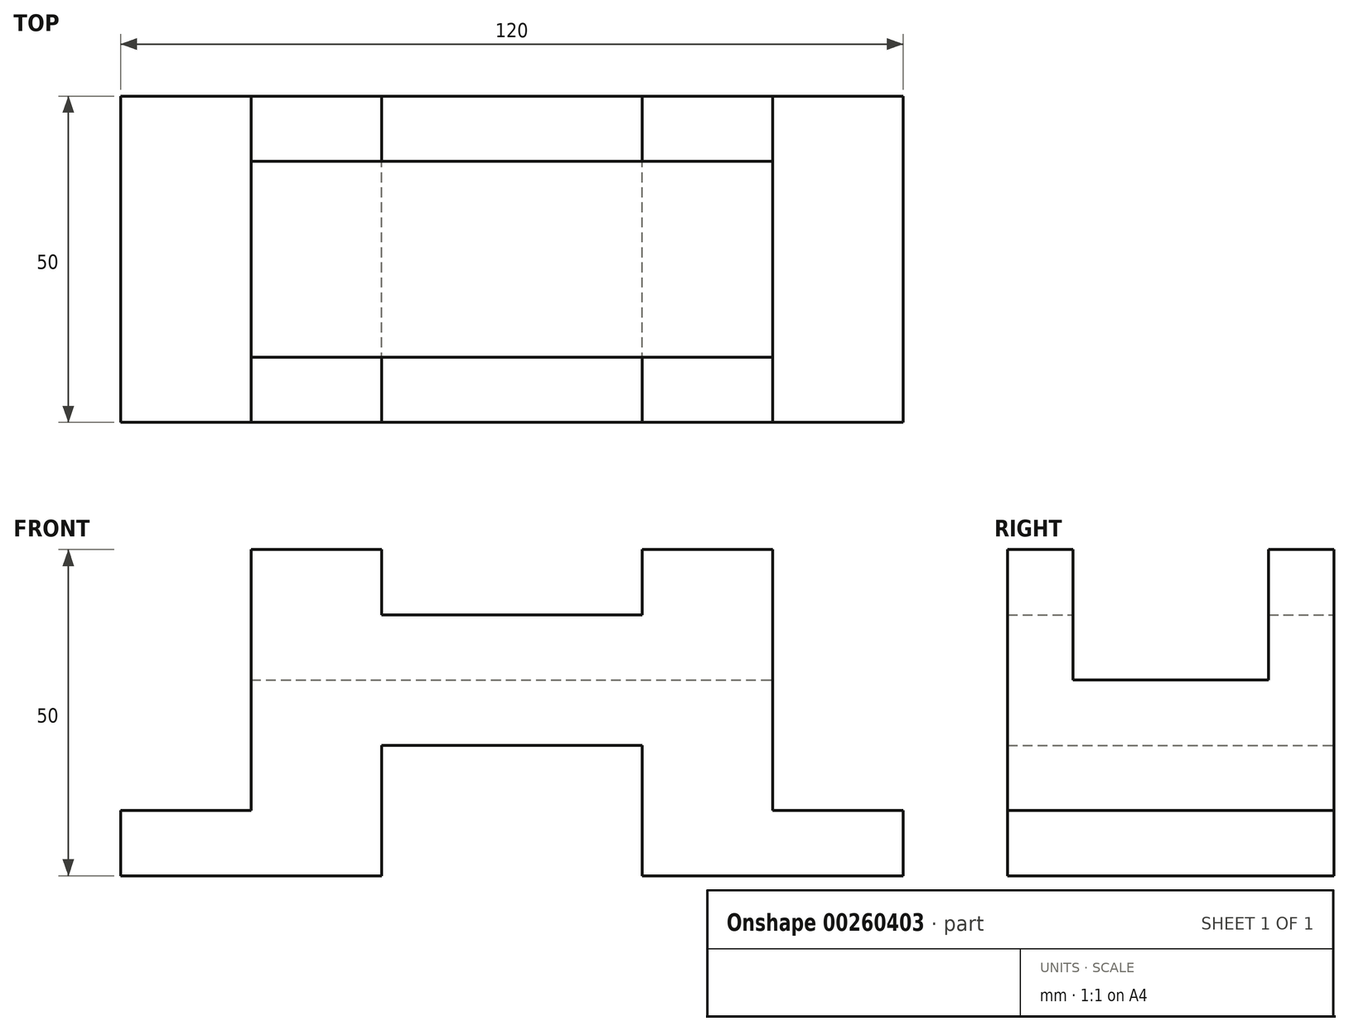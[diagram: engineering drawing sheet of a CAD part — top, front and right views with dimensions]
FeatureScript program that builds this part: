
annotation { "Feature Type Name" : "Feature", "Feature Type Description" : "" }
export const myFeature = defineFeature(function(context is Context, id is Id, definition is map)
    precondition{}
    {
        {
            assignVariable(context, id + "F0", {"name" : "A", "anyValue" : 50});
        }
        {
            var Q0;
            Q0=qCreatedBy(makeId("Front.planeOp"),FACE);
            var sketch = newSketch(context, id + "F1", { "sketchPlane" : qUnion([Q0])});
            skLineSegment(sketch, "E0", {"start": v(-0.57, -0.86) * mm, "end": v(0, 0) * mm});
            skLineSegment(sketch, "E1", {"start": v(-19.8, 0) * mm, "end": v(-19.8, 20) * mm});
            skLineSegment(sketch, "E2", {"start": v(20.2, 0) * mm, "end": v(20.2, 20) * mm});
            skLineSegment(sketch, "E3", {"start": v(-19.8, 20) * mm, "end": v(20.2, 20) * mm});
            skLineSegment(sketch, "E4", {"start": v(-19.8, 0) * mm, "end": v(-59.8, 0) * mm});
            skLineSegment(sketch, "E5", {"start": v(20.2, 0) * mm, "end": v(60.2, 0) * mm});
            skLineSegment(sketch, "E6", {"start": v(-59.8, 0) * mm, "end": v(60.2, 0) * mm});
            skLineSegment(sketch, "E7", {"start": v(60.2, 0) * mm, "end": v(60.2, 10) * mm});
            skLineSegment(sketch, "E8", {"start": v(-59.8, 0) * mm, "end": v(-59.8, 10) * mm});
            skLineSegment(sketch, "E9", {"start": v(60.2, 10) * mm, "end": v(40.2, 10) * mm});
            skLineSegment(sketch, "E10", {"start": v(40.2, 50) * mm, "end": v(40.2, 10) * mm});
            skLineSegment(sketch, "E11", {"start": v(-59.8, 10) * mm, "end": v(-39.8, 10) * mm});
            skLineSegment(sketch, "E12", {"start": v(-39.8, 10) * mm, "end": v(-39.8, 50) * mm});
            skLineSegment(sketch, "E13", {"start": v(-39.8, 50) * mm, "end": v(-19.8, 50) * mm});
            skLineSegment(sketch, "E14", {"start": v(-19.8, 40) * mm, "end": v(20.2, 40) * mm});
            skLineSegment(sketch, "E15", {"start": v(20.2, 40) * mm, "end": v(20.2, 50) * mm});
            skLineSegment(sketch, "E16", {"start": v(20.2, 50) * mm, "end": v(40.2, 50) * mm});
            skLineSegment(sketch, "E17", {"start": v(-19.8, 40) * mm, "end": v(-19.8, 50) * mm});
            skSolve(sketch);
        }
        {
            var Q0;
            {var subQ1=sQuery(id+"F1.wireOp",EDGE,"E1");Q0=makeQuery(id+"F1.imprint","IMPRINT",FACE,{"disambiguationData":[TD([[makeQuery(id+"F1.imprint","IMPRINT",EDGE,{"derivedFrom":subQ1}),1.0]])]});}
            extrude(context, id + "F2", {"entities" : qUnion([Q0]), "endBound" : BoundingType.SYMMETRIC, "depth" : (getVariable(context, 'A')) * mm});
        }
        {
            var Q0;
            Q0=makeQuery(id+"F2.opExtrude","SWEPT_FACE",FACE,{"disambiguationData":[OSD([sQuery(id+"F1.wireOp",EDGE,"E10")])]});
            var sketch = newSketch(context, id + "F3", { "sketchPlane" : qUnion([Q0])});
            skLineSegment(sketch, "E18", {"start": v(15, 50) * mm, "end": v(15, 30) * mm});
            skLineSegment(sketch, "E19", {"start": v(15, 30) * mm, "end": v(-15, 30) * mm});
            skLineSegment(sketch, "E20", {"start": v(-15, 30) * mm, "end": v(-15, 50) * mm});
            skLineSegment(sketch, "E21", {"start": v(-15, 50) * mm, "end": v(-25, 50) * mm});
            skSolve(sketch);
        }
        {
            var Q0;
            {var subQ0=sQuery(id+"F3.wireOp",EDGE,"E18");Q0=makeQuery(id+"F3.imprint","IMPRINT",FACE,{"disambiguationData":[TD([[makeQuery(id+"F3.imprint","IMPRINT",EDGE,{"derivedFrom":subQ0}),-1.0]])]});}
            extrude(context, id + "F4", {"entities" : qUnion([Q0]), "operationType" : NewBodyOperationType.REMOVE, "endBound" : BoundingType.THROUGH_ALL, "oppositeDirection" : true, "depth" : 25 * mm});
        }
    });
